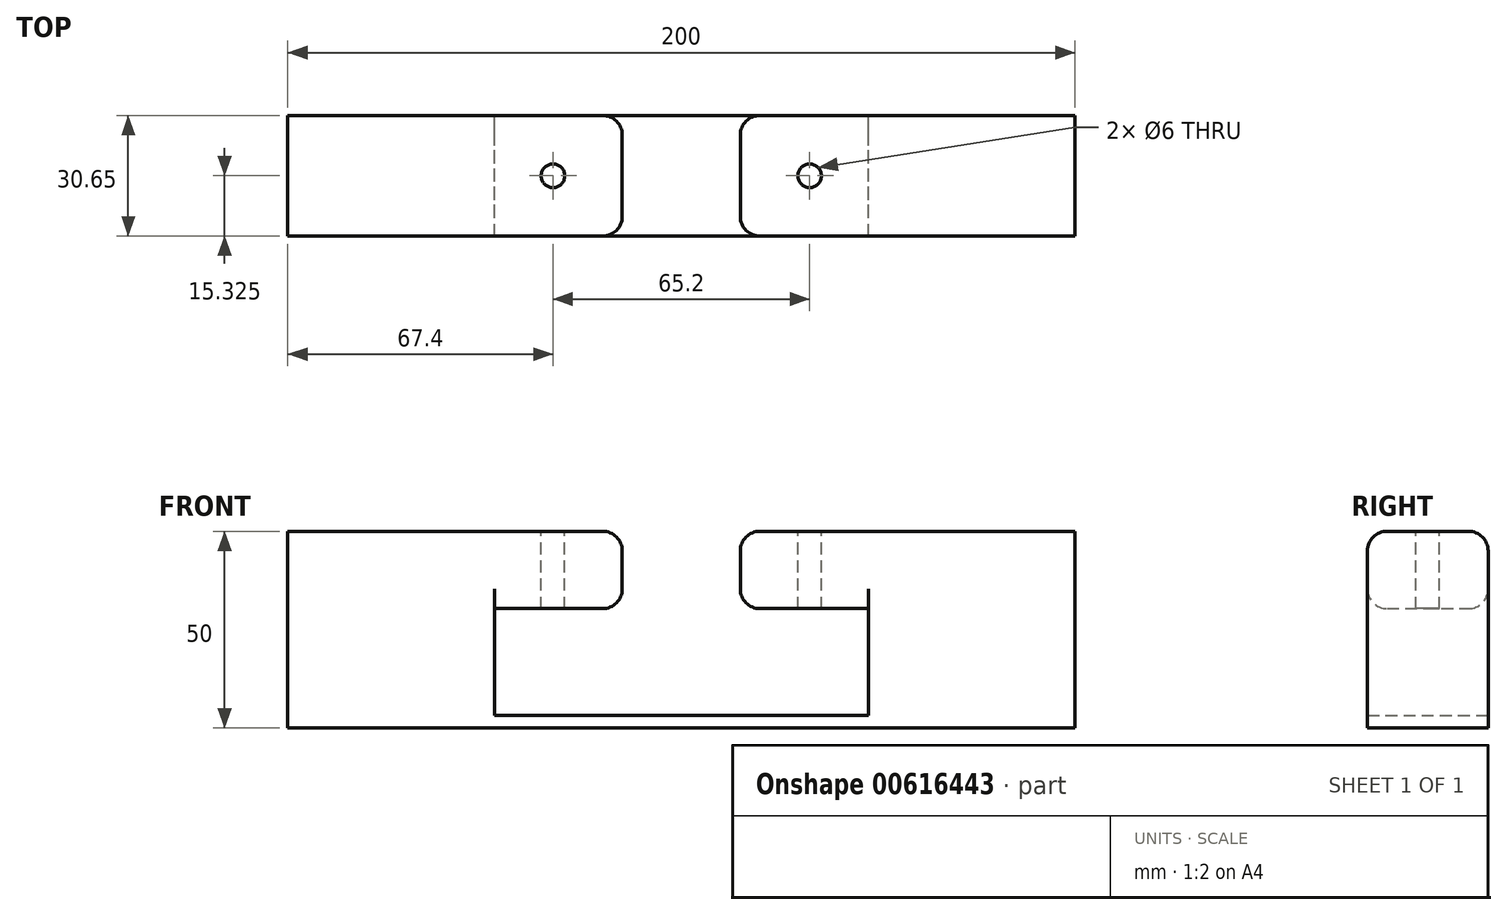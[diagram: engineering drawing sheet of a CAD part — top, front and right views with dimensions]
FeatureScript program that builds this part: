
annotation { "Feature Type Name" : "Feature", "Feature Type Description" : "" }
export const myFeature = defineFeature(function(context is Context, id is Id, definition is map)
    precondition{}
    {
        {
            var Q0;
            Q0=qCreatedBy(makeId("Front.planeOp"),FACE);
            var sketch = newSketch(context, id + "F0", { "sketchPlane" : qUnion([Q0])});
            skLineSegment(sketch, "E0.bottom", {"start": v(-100, -25) * mm, "end": v(100, -25) * mm});
            skLineSegment(sketch, "E0.top", {"start": v(-100, 25) * mm, "end": v(-15, 25) * mm});
            skLineSegment(sketch, "E0.left", {"start": v(-100, -25) * mm, "end": v(-100, 25) * mm});
            skLineSegment(sketch, "E0.right", {"start": v(100, -25) * mm, "end": v(100, 25) * mm});
            skPoint(sketch, "E0.middle", {"position": v(0, 0) * mm});
            skLineSegment(sketch, "E1.left", {"start": v(-15, 25) * mm, "end": v(-15, 5.35) * mm});
            skPoint(sketch, "E1.middle", {"position": v(0, 11.59) * mm});
            skLineSegment(sketch, "E2", {"start": v(-47.5, 5.35) * mm, "end": v(-15, 5.35) * mm});
            skLineSegment(sketch, "E3", {"start": v(-47.5, 5.35) * mm, "end": v(-47.5, -7.07) * mm});
            skLineSegment(sketch, "E4.trimOffspring", {"start": v(12.5, 25) * mm, "end": v(100, 25) * mm});
            skPoint(sketch, "E1.top.end.orphan", {"position": v(15, -9.11) * mm});
            skPoint(sketch, "E1.top.start.orphan", {"position": v(-15, -9.11) * mm});
            skPoint(sketch, "E1.bottom.start.orphan", {"position": v(-15, 32.29) * mm});
            skPoint(sketch, "E1.right.start.orphan", {"position": v(15, 32.29) * mm});
            skLineSegment(sketch, "E5", {"start": v(-47.5, -7.07) * mm, "end": v(-47.5, -21.82) * mm});
            skLineSegment(sketch, "E6", {"start": v(-47.5, -21.82) * mm, "end": v(0, -21.82) * mm});
            skLineSegment(sketch, "E7.MirrorCS", {"start": v(15, 25) * mm, "end": v(15, 5.35) * mm});
            skLineSegment(sketch, "E8.MirrorCS", {"start": v(47.5, 5.35) * mm, "end": v(15, 5.35) * mm});
            skLineSegment(sketch, "E9.MirrorCS", {"start": v(47.5, 5.35) * mm, "end": v(47.5, -7.07) * mm});
            skLineSegment(sketch, "E10.MirrorCS", {"start": v(47.5, -7.07) * mm, "end": v(47.5, -21.82) * mm});
            skLineSegment(sketch, "E11.MirrorCS", {"start": v(47.5, -21.82) * mm, "end": v(0, -21.82) * mm});
            skSolve(sketch);
        }
        {
            var Q0;
            Q0 = qSketchRegion(id + "F0", true);
            extrude(context, id + "F1", {"entities" : qUnion([Q0]), "depth" : 30.65 * mm, "offsetDistance" : 25 * mm});
        }
        {
            var Q0;
            Q0=makeQuery(id+"F1.opExtrude","CAP_EDGE",EDGE,{"disambiguationData":[OSD([sQuery(id+"F0.wireOp",EDGE,"E0.top")])],"isStart":false});
            fillet(context, id + "F2", {"entities" : qUnion([Q0]), "radius" : 5 * mm, "tangentPropagation" : true, "allowEdgeOverflow" : false});
        }
        {
            var Q0;
            Q0=makeQuery(id+"F1.opExtrude","CAP_EDGE",EDGE,{"disambiguationData":[OSD([sQuery(id+"F0.wireOp",EDGE,"E1.left")])],"isStart":false});
            fillet(context, id + "F3", {"entities" : qUnion([Q0]), "radius" : 5 * mm, "tangentPropagation" : true, "allowEdgeOverflow" : false});
        }
        {
            var Q0;
            Q0=makeQuery(id+"F1.opExtrude","CAP_EDGE",EDGE,{"disambiguationData":[OSD([sQuery(id+"F0.wireOp",EDGE,"E2")])],"isStart":false});
            fillet(context, id + "F4", {"entities" : qUnion([Q0]), "radius" : 5 * mm, "tangentPropagation" : true, "allowEdgeOverflow" : false});
        }
        {
            var Q0;
            Q0=makeQuery(id+"F1.opExtrude","CAP_EDGE",EDGE,{"disambiguationData":[OSD([sQuery(id+"F0.wireOp",EDGE,"E7.MirrorCS")])],"isStart":false});
            fillet(context, id + "F5", {"entities" : qUnion([Q0]), "radius" : 5 * mm, "tangentPropagation" : true, "allowEdgeOverflow" : false});
        }
        {
            var Q0;
            Q0=makeQuery(id+"F1.opExtrude","CAP_EDGE",EDGE,{"disambiguationData":[OSD([sQuery(id+"F0.wireOp",EDGE,"E8.MirrorCS")])],"isStart":false});
            fillet(context, id + "F6", {"entities" : qUnion([Q0]), "radius" : 5 * mm, "tangentPropagation" : true, "allowEdgeOverflow" : false});
        }
        {
            var Q0;
            Q0=makeQuery(id+"F1.opExtrude","CAP_EDGE",EDGE,{"disambiguationData":[OSD([sQuery(id+"F0.wireOp",EDGE,"E4.trimOffspring")])],"isStart":false});
            fillet(context, id + "F7", {"entities" : qUnion([Q0]), "radius" : 5 * mm, "tangentPropagation" : true, "allowEdgeOverflow" : false});
        }
        {
            var Q0;
            Q0=makeQuery(id+"F1.opExtrude","CAP_EDGE",EDGE,{"disambiguationData":[OSD([sQuery(id+"F0.wireOp",EDGE,"E4.trimOffspring")])],"isStart":true});
            fillet(context, id + "F8", {"entities" : qUnion([Q0]), "radius" : 5 * mm, "tangentPropagation" : true, "allowEdgeOverflow" : false});
        }
        {
            var Q0;
            Q0=makeQuery(id+"F1.opExtrude","CAP_EDGE",EDGE,{"disambiguationData":[OSD([sQuery(id+"F0.wireOp",EDGE,"E2")])],"isStart":true});
            fillet(context, id + "F9", {"entities" : qUnion([Q0]), "radius" : 5 * mm, "tangentPropagation" : true, "allowEdgeOverflow" : false});
        }
        {
            var Q0;
            Q0=makeQuery(id+"F1.opExtrude","SWEPT_FACE",FACE,{"disambiguationData":[OSD([sQuery(id+"F0.wireOp",EDGE,"E0.top")])]});
            var sketch = newSketch(context, id + "F10", { "sketchPlane" : qUnion([Q0])});
            skCircle(sketch, "E12", {"center": v(-32.6, -15.32) * mm, "radius": 3 * mm});
            skPoint(sketch, "E12.centerSnap0", {"position": v(-20, -15.32) * mm});
            skCircle(sketch, "E13.MirrorC", {"center": v(32.6, -15.32) * mm, "radius": 3 * mm});
            skSolve(sketch);
        }
        {
            var Q0;
            Q0 = qSketchRegion(id + "F10", true);
            extrude(context, id + "F11", {"entities" : qUnion([Q0]), "operationType" : NewBodyOperationType.REMOVE, "oppositeDirection" : true, "depth" : 20 * mm, "offsetDistance" : 25 * mm});
        }
    });
